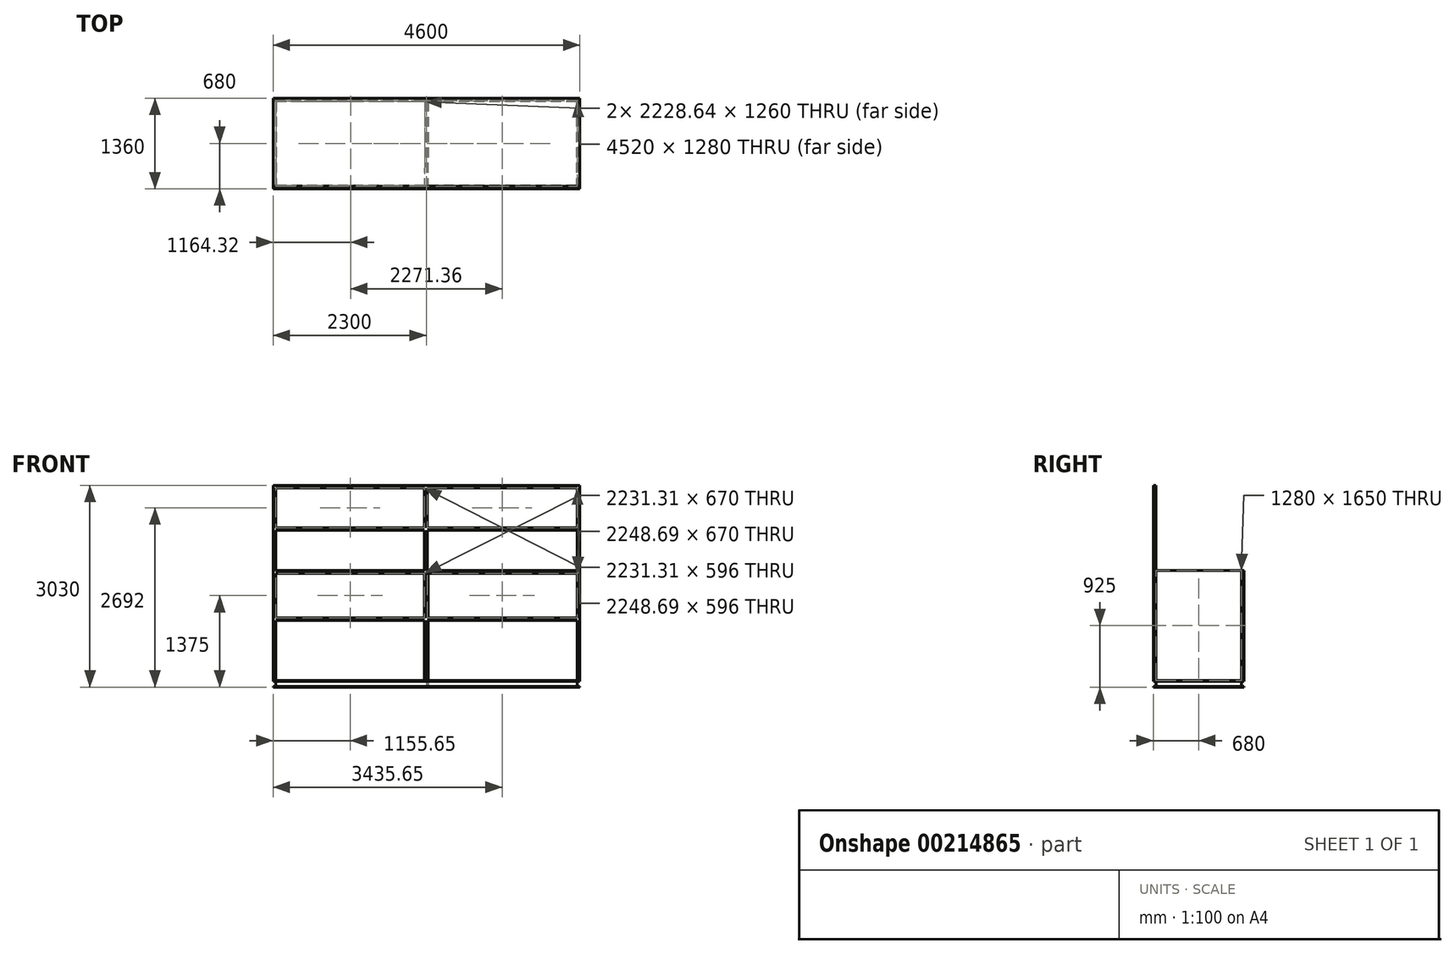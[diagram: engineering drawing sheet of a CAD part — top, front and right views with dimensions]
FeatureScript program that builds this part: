
annotation { "Feature Type Name" : "Feature", "Feature Type Description" : "" }
export const myFeature = defineFeature(function(context is Context, id is Id, definition is map)
    precondition{}
    {
        {
            var Q0;
            Q0=qCreatedBy(makeId("Top.planeOp"),FACE);
            var sketch = newSketch(context, id + "F0", { "sketchPlane" : qUnion([Q0])});
            skLineSegment(sketch, "E0.rect.bottom", {"start": v(2300, 680) * mm, "end": v(-2300, 680) * mm});
            skLineSegment(sketch, "E0.rect.top", {"start": v(2300, -680) * mm, "end": v(-2300, -680) * mm});
            skLineSegment(sketch, "E0.rect.left", {"start": v(2300, 680) * mm, "end": v(2300, -680) * mm});
            skLineSegment(sketch, "E0.rect.right", {"start": v(-2300, 680) * mm, "end": v(-2300, -680) * mm});
            skPoint(sketch, "E0.rect.middle", {"position": v(0, 0) * mm});
            skLineSegment(sketch, "E1.rect.bottom", {"start": v(2250, 630) * mm, "end": v(28.64, 630) * mm});
            skLineSegment(sketch, "E1.rect.top", {"start": v(2250, -630) * mm, "end": v(21.36, -630) * mm});
            skLineSegment(sketch, "E1.rect.left", {"start": v(2250, 630) * mm, "end": v(2250, -630) * mm});
            skLineSegment(sketch, "E1.rect.right", {"start": v(-2250, 630) * mm, "end": v(-2250, -630) * mm});
            skLineSegment(sketch, "E2.rect.left", {"start": v(28.64, 630) * mm, "end": v(21.36, -630) * mm});
            skLineSegment(sketch, "E2.rect.right", {"start": v(-21.36, 630) * mm, "end": v(-28.64, -630) * mm});
            skLineSegment(sketch, "E3.trimOffspring", {"start": v(-21.36, 630) * mm, "end": v(-2250, 630) * mm});
            skLineSegment(sketch, "E4.trimOffspring", {"start": v(-28.64, -630) * mm, "end": v(-2250, -630) * mm});
            skSolve(sketch);
        }
        {
            var Q0;
            Q0=makeQuery(id+"F0.imprint","IMPRINT",FACE,{"disambiguationData":[TD([[makeQuery(id+"F0.imprint","IMPRINT",EDGE,{"derivedFrom":sQuery(id+"F0.wireOp",EDGE,"E0.rect.bottom")}),1.0]])]});
            extrude(context, id + "F1", {"entities" : qUnion([Q0]), "depth" : 100 * mm});
        }
        {
            var Q0;
            Q0=makeQuery(id+"F1.opExtrude","SWEPT_FACE",FACE,{"disambiguationData":[OSD([sQuery(id+"F0.wireOp",EDGE,"E0.rect.right")])]});
            var sketch = newSketch(context, id + "F2", { "sketchPlane" : qUnion([Q0])});
            skLineSegment(sketch, "E5.bottom", {"start": v(-680, 90) * mm, "end": v(-640, 90) * mm});
            skLineSegment(sketch, "E5.top", {"start": v(-680, 10) * mm, "end": v(-640, 10) * mm});
            skLineSegment(sketch, "E5.left", {"start": v(-680, 90) * mm, "end": v(-680, 10) * mm});
            skLineSegment(sketch, "E5.right", {"start": v(-640, 90) * mm, "end": v(-640, 10) * mm});
            skLineSegment(sketch, "E6.bottom", {"start": v(680, 90) * mm, "end": v(640, 90) * mm});
            skLineSegment(sketch, "E6.top", {"start": v(680, 10) * mm, "end": v(640, 10) * mm});
            skLineSegment(sketch, "E6.left", {"start": v(680, 90) * mm, "end": v(680, 10) * mm});
            skLineSegment(sketch, "E6.right", {"start": v(640, 90) * mm, "end": v(640, 10) * mm});
            skSolve(sketch);
        }
        {
            var Q0;
            Q0=makeQuery(id+"F2.imprint","IMPRINT",FACE,{"disambiguationData":[TD([[makeQuery(id+"F2.imprint","IMPRINT",EDGE,{"derivedFrom":sQuery(id+"F2.wireOp",EDGE,"E5.bottom")}),-1.0]])]});
            var Q1;
            Q1=makeQuery(id+"F2.imprint","IMPRINT",FACE,{"disambiguationData":[TD([[makeQuery(id+"F2.imprint","IMPRINT",EDGE,{"derivedFrom":sQuery(id+"F2.wireOp",EDGE,"E6.bottom")}),1.0]])]});
            extrude(context, id + "F3", {"entities" : qUnion([Q0, Q1]), "operationType" : NewBodyOperationType.REMOVE, "endBound" : BoundingType.THROUGH_ALL, "oppositeDirection" : true, "depth" : 25 * mm});
        }
        {
            var Q0;
            Q0=makeQuery(id+"F3.boolean.opBoolean","COPY",FACE,{"derivedFrom":makeQuery(id+"F3.opExtrude","SWEPT_FACE",FACE,{"disambiguationData":[OSD([sQuery(id+"F2.wireOp",EDGE,"E6.right")])]})});
            var sketch = newSketch(context, id + "F4", { "sketchPlane" : qUnion([Q0])});
            skLineSegment(sketch, "E7.bottom", {"start": v(2300, 90) * mm, "end": v(2260, 90) * mm});
            skLineSegment(sketch, "E7.top", {"start": v(2300, 10) * mm, "end": v(2260, 10) * mm});
            skLineSegment(sketch, "E7.left", {"start": v(2300, 90) * mm, "end": v(2300, 10) * mm});
            skLineSegment(sketch, "E7.right", {"start": v(2260, 90) * mm, "end": v(2260, 10) * mm});
            skLineSegment(sketch, "E8.bottom", {"start": v(-2300, 90) * mm, "end": v(-2260, 90) * mm});
            skLineSegment(sketch, "E8.top", {"start": v(-2300, 10) * mm, "end": v(-2260, 10) * mm});
            skLineSegment(sketch, "E8.left", {"start": v(-2300, 90) * mm, "end": v(-2300, 10) * mm});
            skLineSegment(sketch, "E8.right", {"start": v(-2260, 90) * mm, "end": v(-2260, 10) * mm});
            skSolve(sketch);
        }
        {
            var Q0;
            Q0=makeQuery(id+"F4.imprint","IMPRINT",FACE,{"disambiguationData":[TD([[makeQuery(id+"F4.imprint","IMPRINT",EDGE,{"derivedFrom":sQuery(id+"F4.wireOp",EDGE,"E7.bottom")}),1.0]])]});
            var Q1;
            Q1=makeQuery(id+"F4.imprint","IMPRINT",FACE,{"disambiguationData":[TD([[makeQuery(id+"F4.imprint","IMPRINT",EDGE,{"derivedFrom":sQuery(id+"F4.wireOp",EDGE,"E8.bottom")}),1.0]])]});
            extrude(context, id + "F5", {"entities" : qUnion([Q0, Q1]), "operationType" : NewBodyOperationType.REMOVE, "endBound" : BoundingType.THROUGH_ALL, "oppositeDirection" : true, "depth" : 25 * mm});
        }
        {
            var Q0;
            Q0=qCreatedBy(makeId("Top.planeOp"),FACE);
            cPlane(context, id + "F6", {"entities" : qUnion([Q0]), "cplaneType" : CPlaneType.OFFSET, "offset" : 1750 * mm, "width" : 150 * mm, "height" : 150 * mm});
        }
        {
            var Q0;
            Q0=qCreatedBy(makeId("Front.planeOp"),FACE);
            var sketch = newSketch(context, id + "F7", { "sketchPlane" : qUnion([Q0])});
            skLineSegment(sketch, "E9.bottom", {"start": v(0, 10) * mm, "end": v(-90, 10) * mm});
            skLineSegment(sketch, "E9.top", {"start": v(0, 90) * mm, "end": v(-90, 90) * mm});
            skLineSegment(sketch, "E9.left", {"start": v(0, 10) * mm, "end": v(0, 90) * mm});
            skLineSegment(sketch, "E9.right", {"start": v(-90, 10) * mm, "end": v(-90, 90) * mm});
            skSolve(sketch);
        }
        {
            var Q0;
            Q0=qSketchRegion(id+"F7",true);
            var Q1;
            Q1=makeQuery(id+"F1.opExtrude","SWEPT_FACE",FACE,{"disambiguationData":[OSD([sQuery(id+"F0.wireOp",EDGE,"E3.trimOffspring")])]});
            var Q2;
            Q2=makeQuery(id+"F1.opExtrude","SWEPT_FACE",FACE,{"disambiguationData":[OSD([sQuery(id+"F0.wireOp",EDGE,"E4.trimOffspring")])]});
            extrude(context, id + "F8", {"entities" : qUnion([Q0]), "operationType" : NewBodyOperationType.REMOVE, "endBound" : BoundingType.UP_TO_SURFACE, "oppositeDirection" : true, "endBoundEntityFace" : qUnion([Q1]), "depth" : 25 * mm, "hasSecondDirection" : true, "secondDirectionBound" : SecondDirectionBoundingType.UP_TO_SURFACE, "secondDirectionOppositeDirection" : false, "secondDirectionBoundEntityFace" : qUnion([Q2]), "secondDirectionDepth" : 25 * mm});
        }
        {
            var Q0;
            Q0=makeQuery(id+"F1.opExtrude","CAP_FACE",FACE,{"disambiguationData":[OSD([sQuery(id+"F0.wireOp",EDGE,"E0.rect.bottom"),sQuery(id+"F0.wireOp",EDGE,"E0.rect.top"),sQuery(id+"F0.wireOp",EDGE,"E0.rect.left"),sQuery(id+"F0.wireOp",EDGE,"E0.rect.right"),sQuery(id+"F0.wireOp",EDGE,"E1.rect.bottom"),sQuery(id+"F0.wireOp",EDGE,"E1.rect.top"),sQuery(id+"F0.wireOp",EDGE,"E1.rect.left"),sQuery(id+"F0.wireOp",EDGE,"E1.rect.right"),sQuery(id+"F0.wireOp",EDGE,"E2.rect.left"),sQuery(id+"F0.wireOp",EDGE,"E2.rect.right"),sQuery(id+"F0.wireOp",EDGE,"E3.trimOffspring"),sQuery(id+"F0.wireOp",EDGE,"E4.trimOffspring")])],"isStart":false});
            var sketch = newSketch(context, id + "F9", { "sketchPlane" : qUnion([Q0])});
            skLineSegment(sketch, "E10.bottom", {"start": v(-2300, 680) * mm, "end": v(-2260, 680) * mm});
            skLineSegment(sketch, "E10.top", {"start": v(-2300, 640) * mm, "end": v(-2260, 640) * mm});
            skLineSegment(sketch, "E10.left", {"start": v(-2300, 680) * mm, "end": v(-2300, 640) * mm});
            skLineSegment(sketch, "E10.right", {"start": v(-2260, 680) * mm, "end": v(-2260, 640) * mm});
            skLineSegment(sketch, "E11.bottom", {"start": v(2300, 680) * mm, "end": v(2260, 680) * mm});
            skLineSegment(sketch, "E11.top", {"start": v(2300, 640) * mm, "end": v(2260, 640) * mm});
            skLineSegment(sketch, "E11.left", {"start": v(2300, 680) * mm, "end": v(2300, 640) * mm});
            skLineSegment(sketch, "E11.right", {"start": v(2260, 680) * mm, "end": v(2260, 640) * mm});
            skLineSegment(sketch, "E12.bottom", {"start": v(-16.08, 680) * mm, "end": v(23.92, 680) * mm});
            skLineSegment(sketch, "E12.top", {"start": v(-16.3, 640) * mm, "end": v(23.7, 640) * mm});
            skLineSegment(sketch, "E12.left", {"start": v(-16.08, 680) * mm, "end": v(-16.3, 640) * mm});
            skLineSegment(sketch, "E12.right", {"start": v(23.92, 680) * mm, "end": v(23.7, 640) * mm});
            skLineSegment(sketch, "E13.bottom", {"start": v(-2300, -640) * mm, "end": v(-2260, -640) * mm});
            skLineSegment(sketch, "E13.top", {"start": v(-2300, -680) * mm, "end": v(-2260, -680) * mm});
            skLineSegment(sketch, "E13.left", {"start": v(-2300, -640) * mm, "end": v(-2300, -680) * mm});
            skLineSegment(sketch, "E13.right", {"start": v(-2260, -640) * mm, "end": v(-2260, -680) * mm});
            skLineSegment(sketch, "E14.bottom", {"start": v(-28.7, -640) * mm, "end": v(11.3, -640) * mm});
            skLineSegment(sketch, "E14.top", {"start": v(-28.7, -680) * mm, "end": v(11.3, -680) * mm});
            skLineSegment(sketch, "E14.left", {"start": v(-28.7, -640) * mm, "end": v(-28.7, -680) * mm});
            skLineSegment(sketch, "E14.right", {"start": v(11.3, -640) * mm, "end": v(11.3, -680) * mm});
            skLineSegment(sketch, "E15.bottom", {"start": v(2300, -640) * mm, "end": v(2260, -640) * mm});
            skLineSegment(sketch, "E15.top", {"start": v(2300, -680) * mm, "end": v(2260, -680) * mm});
            skLineSegment(sketch, "E15.left", {"start": v(2300, -640) * mm, "end": v(2300, -680) * mm});
            skLineSegment(sketch, "E15.right", {"start": v(2260, -640) * mm, "end": v(2260, -680) * mm});
            skSolve(sketch);
        }
        {
            var Q0;
            Q0=makeQuery(id+"F9.imprint","IMPRINT",FACE,{"disambiguationData":[TD([[makeQuery(id+"F9.imprint","IMPRINT",EDGE,{"derivedFrom":sQuery(id+"F9.wireOp",EDGE,"E13.bottom")}),-1.0]])]});
            var Q1;
            Q1=makeQuery(id+"F9.imprint","IMPRINT",FACE,{"disambiguationData":[TD([[makeQuery(id+"F9.imprint","IMPRINT",EDGE,{"derivedFrom":sQuery(id+"F9.wireOp",EDGE,"E15.bottom")}),1.0]])]});
            var Q2;
            Q2=makeQuery(id+"F9.imprint","IMPRINT",FACE,{"disambiguationData":[TD([[makeQuery(id+"F9.imprint","IMPRINT",EDGE,{"derivedFrom":sQuery(id+"F9.wireOp",EDGE,"E14.bottom")}),-1.0]])]});
            extrude(context, id + "F10", {"entities" : qUnion([Q0, Q1, Q2]), "operationType" : NewBodyOperationType.ADD, "depth" : 2930 * mm});
        }
        {
            var Q0;
            Q0=qCreatedBy(id+"F6.planeOp",FACE);
            var sketch = newSketch(context, id + "F11", { "sketchPlane" : qUnion([Q0])});
            skLineSegment(sketch, "E16.bottom", {"start": v(-2300, 680) * mm, "end": v(2300, 680) * mm});
            skLineSegment(sketch, "E16.top", {"start": v(-2300, -680) * mm, "end": v(2300, -680) * mm});
            skLineSegment(sketch, "E16.left", {"start": v(-2300, 680) * mm, "end": v(-2300, -680) * mm});
            skLineSegment(sketch, "E16.right", {"start": v(2300, 680) * mm, "end": v(2300, -680) * mm});
            skSolve(sketch);
        }
        {
            var Q0;
            Q0=qSketchRegion(id+"F11",true);
            extrude(context, id + "F12", {"entities" : qUnion([Q0]), "operationType" : NewBodyOperationType.ADD, "depth" : 4 * mm});
        }
        {
            var Q0;
            Q0=qSketchRegion(id+"F9",true);
            extrude(context, id + "F13", {"entities" : qUnion([Q0]), "operationType" : NewBodyOperationType.ADD, "depth" : 1650 * mm});
        }
        {
            var Q0;
            {var subQ1=sQuery(id+"F0.wireOp",EDGE,"E0.rect.left");Q0=makeQuery(id+"F12.boolean.opBoolean","MERGE",FACE,{"derivedFrom":[makeQuery(id+"F10.boolean.opBoolean","MERGE",FACE,{"derivedFrom":[makeQuery(id+"F5.boolean.opBoolean","SPLIT",FACE,{"disambiguationData":[TD([makeQuery(id+"F3.boolean.opBoolean","COPY",FACE,{"derivedFrom":makeQuery(id+"F3.opExtrude","SWEPT_FACE",FACE,{"disambiguationData":[OSD([sQuery(id+"F2.wireOp",EDGE,"E5.bottom")])]})})])],"derivedFrom":makeQuery(id+"F1.opExtrude","SWEPT_FACE",FACE,{"disambiguationData":[OSD([subQ1])]})}),makeQuery(id+"F10.opExtrude","SWEPT_FACE",FACE,{"disambiguationData":[OSD([sQuery(id+"F9.wireOp",EDGE,"E11.left")])]}),makeQuery(id+"F10.opExtrude","SWEPT_FACE",FACE,{"disambiguationData":[OSD([sQuery(id+"F9.wireOp",EDGE,"E15.left")])]})]}),makeQuery(id+"F12.opExtrude","SWEPT_FACE",FACE,{"disambiguationData":[OSD([sQuery(id+"F11.wireOp",EDGE,"E16.right")])]})]});}
            var sketch = newSketch(context, id + "F14", { "sketchPlane" : qUnion([Q0])});
            skLineSegment(sketch, "E17.bottom", {"start": v(-680, 3030) * mm, "end": v(-640, 3030) * mm});
            skLineSegment(sketch, "E17.top", {"start": v(-680, 2990) * mm, "end": v(-640, 2990) * mm});
            skLineSegment(sketch, "E17.left", {"start": v(-640, 3030) * mm, "end": v(-640, 2990) * mm});
            skLineSegment(sketch, "E17.right", {"start": v(-680, 3030) * mm, "end": v(-680, 2990) * mm});
            skLineSegment(sketch, "E18.left", {"start": v(680, 1040) * mm, "end": v(680, 1000) * mm});
            skLineSegment(sketch, "E18.right", {"start": v(-640, 1040) * mm, "end": v(-640, 1000) * mm});
            skLineSegment(sketch, "E19.bottom", {"start": v(-680, 1040) * mm, "end": v(-640, 1040) * mm});
            skLineSegment(sketch, "E19.top", {"start": v(-680, 1000) * mm, "end": v(-640, 1000) * mm});
            skLineSegment(sketch, "E19.right", {"start": v(-680, 1040) * mm, "end": v(-680, 1000) * mm});
            skLineSegment(sketch, "E20.bottom", {"start": v(-680, 1750) * mm, "end": v(-640, 1750) * mm});
            skLineSegment(sketch, "E20.top", {"start": v(-680, 1710) * mm, "end": v(-640, 1710) * mm});
            skLineSegment(sketch, "E20.left", {"start": v(-640, 1750) * mm, "end": v(-640, 1710) * mm});
            skLineSegment(sketch, "E20.right", {"start": v(-680, 1750) * mm, "end": v(-680, 1710) * mm});
            skLineSegment(sketch, "E21", {"start": v(640, 1040) * mm, "end": v(680, 1040) * mm});
            skLineSegment(sketch, "E22", {"start": v(640, 1040) * mm, "end": v(640, 1000) * mm});
            skLineSegment(sketch, "E23", {"start": v(680, 1000) * mm, "end": v(640, 1000) * mm});
            skLineSegment(sketch, "E24.bottom", {"start": v(640, 1750) * mm, "end": v(680, 1750) * mm});
            skLineSegment(sketch, "E24.top", {"start": v(640, 1710) * mm, "end": v(680, 1710) * mm});
            skLineSegment(sketch, "E24.left", {"start": v(640, 1750) * mm, "end": v(640, 1710) * mm});
            skLineSegment(sketch, "E24.right", {"start": v(680, 1750) * mm, "end": v(680, 1710) * mm});
            skLineSegment(sketch, "E25.bottom", {"start": v(-680, 2394) * mm, "end": v(-640, 2394) * mm});
            skLineSegment(sketch, "E25.top", {"start": v(-680, 2354) * mm, "end": v(-640, 2354) * mm});
            skLineSegment(sketch, "E25.left", {"start": v(-680, 2394) * mm, "end": v(-680, 2354) * mm});
            skLineSegment(sketch, "E25.right", {"start": v(-640, 2394) * mm, "end": v(-640, 2354) * mm});
            skSolve(sketch);
        }
        {
            var Q0;
            Q0=makeQuery(id+"F14.imprint","IMPRINT",FACE,{"disambiguationData":[TD([[makeQuery(id+"F14.imprint","IMPRINT",EDGE,{"derivedFrom":sQuery(id+"F14.wireOp",EDGE,"E17.bottom")}),1.0]])]});
            var Q1;
            Q1=makeQuery(id+"F14.imprint","IMPRINT",FACE,{"disambiguationData":[TD([[makeQuery(id+"F14.imprint","IMPRINT",EDGE,{"derivedFrom":sQuery(id+"F14.wireOp",EDGE,"E18.left")}),-1.0]])]});
            var Q2;
            Q2=makeQuery(id+"F14.imprint","IMPRINT",FACE,{"disambiguationData":[TD([[makeQuery(id+"F14.imprint","IMPRINT",EDGE,{"derivedFrom":sQuery(id+"F14.wireOp",EDGE,"E19.bottom")}),-1.0]])]});
            var Q3;
            Q3=makeQuery(id+"F14.imprint","IMPRINT",FACE,{"disambiguationData":[TD([[makeQuery(id+"F14.imprint","IMPRINT",EDGE,{"derivedFrom":sQuery(id+"F14.wireOp",EDGE,"E25.bottom")}),-1.0]])]});
            var Q4;
            Q4=makeQuery(id+"F14.imprint","IMPRINT",FACE,{"disambiguationData":[TD([[makeQuery(id+"F14.imprint","IMPRINT",EDGE,{"derivedFrom":sQuery(id+"F14.wireOp",EDGE,"E20.bottom")}),-1.0]])]});
            var Q5;
            Q5=makeQuery(id+"F14.imprint","IMPRINT",FACE,{"disambiguationData":[TD([[makeQuery(id+"F14.imprint","IMPRINT",EDGE,{"derivedFrom":sQuery(id+"F14.wireOp",EDGE,"E24.bottom")}),-1.0]])]});
            var Q6;
            Q6=makeQuery(id+"F10.opExtrude","SWEPT_FACE",FACE,{"disambiguationData":[OSD([sQuery(id+"F9.wireOp",EDGE,"E13.right")])]});
            extrude(context, id + "F15", {"entities" : qUnion([Q0, Q1, Q2, Q3, Q4, Q5]), "operationType" : NewBodyOperationType.ADD, "endBound" : BoundingType.UP_TO_SURFACE, "oppositeDirection" : true, "endBoundEntityFace" : qUnion([Q6]), "depth" : 4300 * mm});
        }
    });
